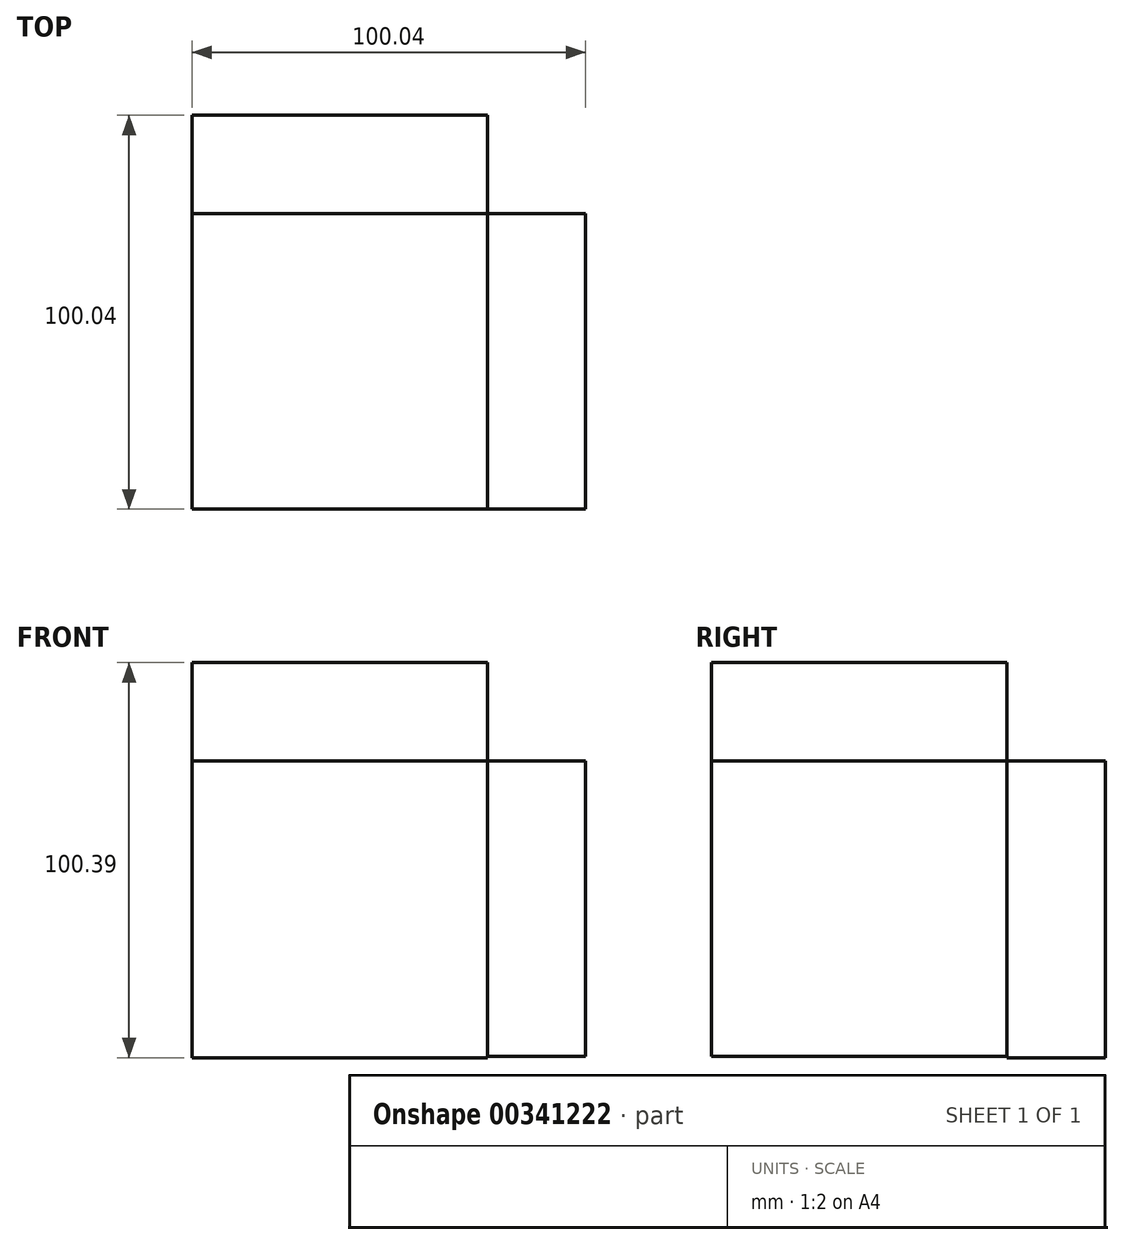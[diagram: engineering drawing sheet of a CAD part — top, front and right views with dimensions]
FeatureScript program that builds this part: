
annotation { "Feature Type Name" : "Feature", "Feature Type Description" : "" }
export const myFeature = defineFeature(function(context is Context, id is Id, definition is map)
    precondition{}
    {
        {
            var Q0;
            Q0=qCreatedBy(makeId("Top.planeOp"),FACE);
            var sketch = newSketch(context, id + "F0", { "sketchPlane" : qUnion([Q0])});
            skLineSegment(sketch, "E0.bottom", {"start": v(0, 0) * mm, "end": v(-75.04, 0) * mm});
            skLineSegment(sketch, "E0.top", {"start": v(0, -75.04) * mm, "end": v(-75.04, -75.04) * mm});
            skLineSegment(sketch, "E0.left", {"start": v(0, 0) * mm, "end": v(0, -75.04) * mm});
            skLineSegment(sketch, "E0.right", {"start": v(-75.04, 0) * mm, "end": v(-75.04, -75.04) * mm});
            skLineSegment(sketch, "E1", {"start": v(-75.04, 0) * mm, "end": v(-75.04, -75.04) * mm, "construction": true});
            skLineSegment(sketch, "E2", {"start": v(-75.04, -75.04) * mm, "end": v(0, -75.04) * mm});
            skLineSegment(sketch, "E3", {"start": v(0, -75.04) * mm, "end": v(0, 0) * mm, "construction": true});
            skLineSegment(sketch, "E4", {"start": v(0, 0) * mm, "end": v(-75.04, 0) * mm, "construction": true});
            skSolve(sketch);
        }
        {
            var Q0;
            Q0=qCreatedBy(makeId("Right.planeOp"),FACE);
            var sketch = newSketch(context, id + "F1", { "sketchPlane" : qUnion([Q0])});
            skLineSegment(sketch, "E5.bottom", {"start": v(0, 0) * mm, "end": v(-75.04, 0) * mm});
            skLineSegment(sketch, "E5.top", {"start": v(0, -75.04) * mm, "end": v(-75.04, -75.04) * mm});
            skLineSegment(sketch, "E5.left", {"start": v(0, 0) * mm, "end": v(0, -75.04) * mm});
            skLineSegment(sketch, "E5.right", {"start": v(-75.04, 0) * mm, "end": v(-75.04, -75.04) * mm});
            skSolve(sketch);
        }
        {
            var Q0;
            Q0=qCreatedBy(makeId("Front.planeOp"),FACE);
            var sketch = newSketch(context, id + "F2", { "sketchPlane" : qUnion([Q0])});
            skLineSegment(sketch, "E6.left", {"start": v(0, 0) * mm, "end": v(0, -75.04) * mm});
            skLineSegment(sketch, "E7.bottom", {"start": v(0, 0) * mm, "end": v(-75.04, 0) * mm});
            skLineSegment(sketch, "E7.top", {"start": v(0, -75.4) * mm, "end": v(-75.04, -75.4) * mm});
            skLineSegment(sketch, "E7.left", {"start": v(0, 0) * mm, "end": v(0, -75.4) * mm});
            skLineSegment(sketch, "E7.right", {"start": v(-75.04, 0) * mm, "end": v(-75.04, -75.4) * mm});
            skLineSegment(sketch, "E8", {"start": v(0, 0) * mm, "end": v(0, -75.04) * mm, "construction": true});
            skLineSegment(sketch, "E9", {"start": v(0, -75.04) * mm, "end": v(-75.04, -75.4) * mm, "construction": true});
            skLineSegment(sketch, "E10", {"start": v(-75.04, -75.4) * mm, "end": v(-75.04, 0) * mm, "construction": true});
            skLineSegment(sketch, "E11", {"start": v(-75.04, 0) * mm, "end": v(0, 0) * mm, "construction": true});
            skLineSegment(sketch, "E12", {"start": v(0, -75.4) * mm, "end": v(0, 0) * mm, "construction": true});
            skSolve(sketch);
        }
        {
            var Q0;
            Q0 = qSketchRegion(id + "F2", true);
            extrude(context, id + "F3", {"entities" : qUnion([Q0]), "oppositeDirection" : true, "depth" : 25 * mm});
        }
        {
            var Q0;
            Q0=makeQuery(id+"F1.imprint","IMPRINT",FACE,{"disambiguationData":[TD([[makeQuery(id+"F1.imprint","IMPRINT",EDGE,{"derivedFrom":sQuery(id+"F1.wireOp",EDGE,"E5.bottom")}),1.0]])]});
            extrude(context, id + "F4", {"entities" : qUnion([Q0]), "depth" : 25 * mm});
        }
        {
            var Q0;
            Q0=makeQuery(id+"F0.imprint","IMPRINT",FACE,{"disambiguationData":[TD([[makeQuery(id+"F0.imprint","IMPRINT",EDGE,{"derivedFrom":sQuery(id+"F0.wireOp",EDGE,"E0.bottom")}),1.0]])]});
            extrude(context, id + "F5", {"entities" : qUnion([Q0]), "depth" : 25 * mm});
        }
    });
